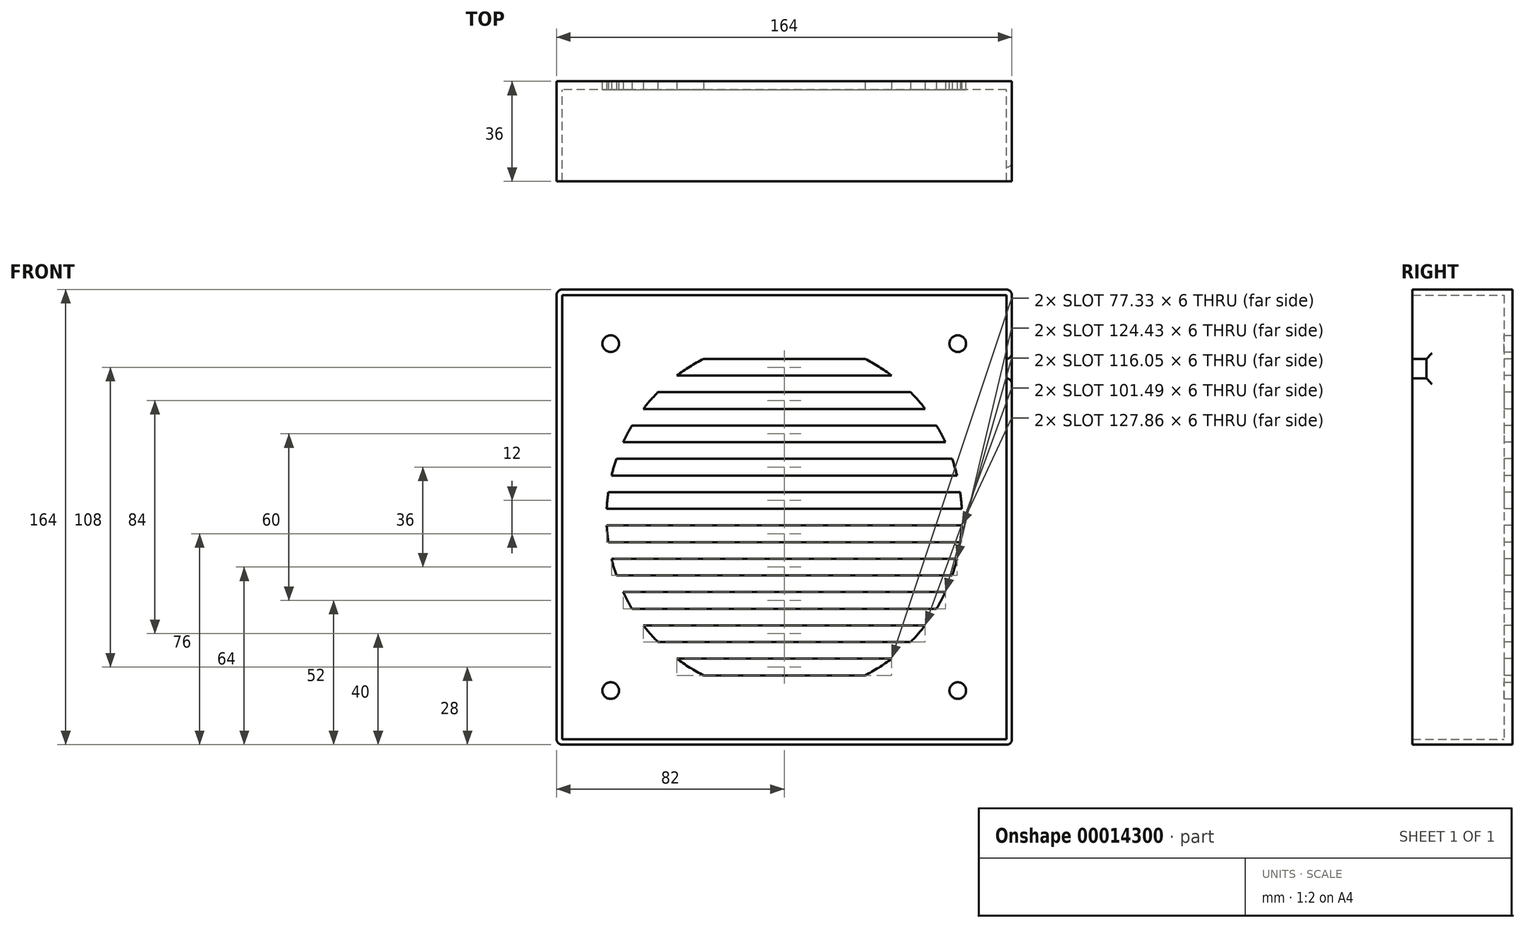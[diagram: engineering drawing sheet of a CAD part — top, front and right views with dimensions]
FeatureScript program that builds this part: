
annotation { "Feature Type Name" : "Feature", "Feature Type Description" : "" }
export const myFeature = defineFeature(function(context is Context, id is Id, definition is map)
    precondition{}
    {
        {
            var Q0;
            Q0=qCreatedBy(makeId("Front.planeOp"),FACE);
            var sketch = newSketch(context, id + "F0", { "sketchPlane" : qUnion([Q0])});
            skLineSegment(sketch, "E0.rect.bottom", {"start": v(-82, 82) * mm, "end": v(82, 82) * mm});
            skLineSegment(sketch, "E0.rect.top", {"start": v(-82, -82) * mm, "end": v(82, -82) * mm});
            skLineSegment(sketch, "E0.rect.left", {"start": v(-82, 82) * mm, "end": v(-82, -82) * mm});
            skLineSegment(sketch, "E0.rect.right", {"start": v(82, 82) * mm, "end": v(82, -82) * mm});
            skPoint(sketch, "E0.rect.middle", {"position": v(0, 0) * mm});
            skCircle(sketch, "E1", {"center": v(-62.5, 62.5) * mm, "radius": 3 * mm});
            skCircle(sketch, "E2", {"center": v(62.5, 62.5) * mm, "radius": 3 * mm});
            skCircle(sketch, "E3", {"center": v(62.5, -62.5) * mm, "radius": 3 * mm});
            skCircle(sketch, "E4", {"center": v(-62.5, -62.5) * mm, "radius": 3 * mm});
            skLineSegment(sketch, "E5", {"start": v(-62.5, 62.5) * mm, "end": v(62.5, 62.5) * mm, "construction": true});
            skLineSegment(sketch, "E6", {"start": v(62.5, 62.5) * mm, "end": v(62.5, -62.5) * mm, "construction": true});
            skLineSegment(sketch, "E7", {"start": v(-62.5, -62.5) * mm, "end": v(62.5, -62.5) * mm, "construction": true});
            skLineSegment(sketch, "E8", {"start": v(-62.5, -62.5) * mm, "end": v(-62.5, 62.5) * mm, "construction": true});
            skLineSegment(sketch, "E9", {"start": v(-62.5, -62.5) * mm, "end": v(-62.5, -82) * mm, "construction": true});
            skLineSegment(sketch, "E10", {"start": v(-62.5, -62.5) * mm, "end": v(-82, -62.5) * mm, "construction": true});
            skLineSegment(sketch, "E11", {"start": v(62.5, 62.5) * mm, "end": v(62.5, 82) * mm, "construction": true});
            skLineSegment(sketch, "E12", {"start": v(62.5, 62.5) * mm, "end": v(82, 62.5) * mm, "construction": true});
            skSolve(sketch);
        }
        {
            var Q0;
            Q0 = qSketchRegion(id + "F0", true);
            extrude(context, id + "F1", {"entities" : qUnion([Q0]), "depth" : 3 * mm});
        }
        {
            var Q0;
            Q0=makeQuery(id+"F1.opExtrude","CAP_FACE",FACE,{"disambiguationData":[OSD([sQuery(id+"F0.wireOp",EDGE,"E0.rect.bottom"),sQuery(id+"F0.wireOp",EDGE,"E0.rect.top"),sQuery(id+"F0.wireOp",EDGE,"E0.rect.left"),sQuery(id+"F0.wireOp",EDGE,"E0.rect.right")])],"isStart":false});
            var sketch = newSketch(context, id + "F2", { "sketchPlane" : qUnion([Q0])});
            skLineSegment(sketch, "E13.rect.bottom", {"start": v(80, 80) * mm, "end": v(-80, 80) * mm});
            skLineSegment(sketch, "E13.rect.top", {"start": v(80, -80) * mm, "end": v(-80, -80) * mm});
            skLineSegment(sketch, "E13.rect.left", {"start": v(80, 80) * mm, "end": v(80, -80) * mm});
            skLineSegment(sketch, "E13.rect.right", {"start": v(-80, 80) * mm, "end": v(-80, -80) * mm});
            skPoint(sketch, "E13.rect.middle", {"position": v(0, 0) * mm});
            skLineSegment(sketch, "E14.rect.bottom", {"start": v(-82, 82) * mm, "end": v(82, 82) * mm});
            skLineSegment(sketch, "E14.rect.top", {"start": v(-82, -82) * mm, "end": v(82, -82) * mm});
            skLineSegment(sketch, "E14.rect.left", {"start": v(-82, 82) * mm, "end": v(-82, -82) * mm});
            skLineSegment(sketch, "E14.rect.right", {"start": v(82, 82) * mm, "end": v(82, -82) * mm});
            skLineSegment(sketch, "E15", {"start": v(-80, 80) * mm, "end": v(-80, 82) * mm, "construction": true});
            skLineSegment(sketch, "E16", {"start": v(-80, 73.83) * mm, "end": v(-82, 73.83) * mm, "construction": true});
            skLineSegment(sketch, "E17", {"start": v(-80, 67.42) * mm, "end": v(80, 67.42) * mm, "construction": true});
            skSolve(sketch);
        }
        {
            var Q0;
            Q0=makeQuery(id+"F2.imprint","IMPRINT",FACE,{"disambiguationData":[TD([[makeQuery(id+"F2.imprint","IMPRINT",EDGE,{"derivedFrom":sQuery(id+"F2.wireOp",EDGE,"E13.rect.bottom")}),-1.0]])]});
            extrude(context, id + "F3", {"entities" : qUnion([Q0]), "operationType" : NewBodyOperationType.ADD, "depth" : 28 * mm});
        }
        {
            var Q0;
            Q0=makeQuery(id+"F1.opExtrude","CAP_FACE",FACE,{"disambiguationData":[OSD([sQuery(id+"F0.wireOp",EDGE,"E0.rect.bottom"),sQuery(id+"F0.wireOp",EDGE,"E0.rect.top"),sQuery(id+"F0.wireOp",EDGE,"E0.rect.left"),sQuery(id+"F0.wireOp",EDGE,"E0.rect.right")])],"isStart":false});
            var sketch = newSketch(context, id + "F4", { "sketchPlane" : qUnion([Q0])});
            skCircle(sketch, "E18", {"center": v(0, 0) * mm, "radius": 64 * mm});
            skLineSegment(sketch, "E19", {"start": v(-63.93, 3) * mm, "end": v(63.93, 3) * mm});
            skLineSegment(sketch, "E20", {"start": v(-63.93, -3) * mm, "end": v(63.93, -3) * mm});
            skLineSegment(sketch, "E21", {"start": v(-63.36, 9) * mm, "end": v(63.36, 9) * mm});
            skLineSegment(sketch, "E22", {"start": v(-62.22, 15) * mm, "end": v(62.22, 15) * mm});
            skLineSegment(sketch, "E23", {"start": v(-63.36, -9) * mm, "end": v(63.36, -9) * mm});
            skLineSegment(sketch, "E24", {"start": v(-60.46, 21) * mm, "end": v(60.46, 21) * mm});
            skLineSegment(sketch, "E25", {"start": v(-58.03, 27) * mm, "end": v(58.03, 27) * mm});
            skLineSegment(sketch, "E26", {"start": v(-50.74, 39) * mm, "end": v(50.74, 39) * mm});
            skLineSegment(sketch, "E27", {"start": v(-45.5, 45) * mm, "end": v(45.5, 45) * mm});
            skLineSegment(sketch, "E28", {"start": v(-38.67, 51) * mm, "end": v(38.67, 51) * mm});
            skLineSegment(sketch, "E29", {"start": v(-29.1, 57) * mm, "end": v(29.1, 57) * mm});
            skLineSegment(sketch, "E30", {"start": v(-62.22, -15) * mm, "end": v(62.22, -15) * mm});
            skLineSegment(sketch, "E31", {"start": v(-60.46, -21) * mm, "end": v(60.46, -21) * mm});
            skLineSegment(sketch, "E32", {"start": v(-58.03, -27) * mm, "end": v(58.03, -27) * mm});
            skLineSegment(sketch, "E33", {"start": v(-54.84, -33) * mm, "end": v(54.84, -33) * mm});
            skLineSegment(sketch, "E34", {"start": v(-50.74, -39) * mm, "end": v(50.74, -39) * mm});
            skLineSegment(sketch, "E35", {"start": v(-45.5, -45) * mm, "end": v(45.5, -45) * mm});
            skLineSegment(sketch, "E36", {"start": v(-38.67, -51) * mm, "end": v(38.67, -51) * mm});
            skLineSegment(sketch, "E37", {"start": v(-29.1, -57) * mm, "end": v(29.1, -57) * mm});
            skLineSegment(sketch, "E38", {"start": v(-54.84, 33) * mm, "end": v(54.84, 33) * mm});
            skSolve(sketch);
        }
        {
            var Q0;
            {var subQ1=sQuery(id+"F4.wireOp",EDGE,"E19");Q0=makeQuery(id+"F4.imprint","IMPRINT",FACE,{"disambiguationData":[TD([[makeQuery(id+"F4.imprint","IMPRINT",EDGE,{"derivedFrom":subQ1}),1.0]])]});}
            var Q1;
            {var subQ1=sQuery(id+"F4.wireOp",EDGE,"E20");Q1=makeQuery(id+"F4.imprint","IMPRINT",FACE,{"disambiguationData":[TD([[makeQuery(id+"F4.imprint","IMPRINT",EDGE,{"derivedFrom":subQ1}),-1.0]])]});}
            var Q2;
            {var subQ0=sQuery(id+"F4.wireOp",EDGE,"E22");Q2=makeQuery(id+"F4.imprint","IMPRINT",FACE,{"disambiguationData":[TD([[makeQuery(id+"F4.imprint","IMPRINT",EDGE,{"derivedFrom":subQ0}),1.0]])]});}
            var Q3;
            {var subQ1=sQuery(id+"F4.wireOp",EDGE,"E30");Q3=makeQuery(id+"F4.imprint","IMPRINT",FACE,{"disambiguationData":[TD([[makeQuery(id+"F4.imprint","IMPRINT",EDGE,{"derivedFrom":subQ1}),-1.0]])]});}
            var Q4;
            {var subQ1=sQuery(id+"F4.wireOp",EDGE,"E32");Q4=makeQuery(id+"F4.imprint","IMPRINT",FACE,{"disambiguationData":[TD([[makeQuery(id+"F4.imprint","IMPRINT",EDGE,{"derivedFrom":subQ1}),-1.0]])]});}
            var Q5;
            {var subQ1=sQuery(id+"F4.wireOp",EDGE,"E34");Q5=makeQuery(id+"F4.imprint","IMPRINT",FACE,{"disambiguationData":[TD([[makeQuery(id+"F4.imprint","IMPRINT",EDGE,{"derivedFrom":subQ1}),-1.0]])]});}
            var Q6;
            {var subQ1=sQuery(id+"F4.wireOp",EDGE,"E36");Q6=makeQuery(id+"F4.imprint","IMPRINT",FACE,{"disambiguationData":[TD([[makeQuery(id+"F4.imprint","IMPRINT",EDGE,{"derivedFrom":subQ1}),-1.0]])]});}
            var Q7;
            {var subQ1=sQuery(id+"F4.wireOp",EDGE,"E25");Q7=makeQuery(id+"F4.imprint","IMPRINT",FACE,{"disambiguationData":[TD([[makeQuery(id+"F4.imprint","IMPRINT",EDGE,{"derivedFrom":subQ1}),1.0]])]});}
            var Q8;
            {var subQ1=sQuery(id+"F4.wireOp",EDGE,"E26");Q8=makeQuery(id+"F4.imprint","IMPRINT",FACE,{"disambiguationData":[TD([[makeQuery(id+"F4.imprint","IMPRINT",EDGE,{"derivedFrom":subQ1}),1.0]])]});}
            var Q9;
            {var subQ1=sQuery(id+"F4.wireOp",EDGE,"E28");Q9=makeQuery(id+"F4.imprint","IMPRINT",FACE,{"disambiguationData":[TD([[makeQuery(id+"F4.imprint","IMPRINT",EDGE,{"derivedFrom":subQ1}),1.0]])]});}
            extrude(context, id + "F5", {"entities" : qUnion([Q0, Q1, Q2, Q3, Q4, Q5, Q6, Q7, Q8, Q9]), "operationType" : NewBodyOperationType.REMOVE, "oppositeDirection" : true, "depth" : 5 * mm});
        }
        {
            var Q0;
            Q0=makeQuery(id+"F3.boolean.opBoolean","MERGE",EDGE,{"derivedFrom":[makeQuery(id+"F1.opExtrude","SWEPT_EDGE",EDGE,{"disambiguationData":[OSD([sQuery(id+"F0.wireOp",EDGE,"E0.rect.bottom"),sQuery(id+"F0.wireOp",EDGE,"E0.rect.left")])]}),makeQuery(id+"F3.opExtrude","SWEPT_EDGE",EDGE,{"disambiguationData":[OSD([sQuery(id+"F2.wireOp",EDGE,"E14.rect.bottom"),sQuery(id+"F2.wireOp",EDGE,"E14.rect.left")])]})]});
            fillet(context, id + "F6", {"entities" : qUnion([Q0]), "radius" : 2 * mm, "tangentPropagation" : true, "allowEdgeOverflow" : false});
        }
        {
            var Q0;
            Q0=makeQuery(id+"F3.boolean.opBoolean","MERGE",EDGE,{"derivedFrom":[makeQuery(id+"F1.opExtrude","SWEPT_EDGE",EDGE,{"disambiguationData":[OSD([sQuery(id+"F0.wireOp",EDGE,"E0.rect.bottom"),sQuery(id+"F0.wireOp",EDGE,"E0.rect.right")])]}),makeQuery(id+"F3.opExtrude","SWEPT_EDGE",EDGE,{"disambiguationData":[OSD([sQuery(id+"F2.wireOp",EDGE,"E14.rect.bottom"),sQuery(id+"F2.wireOp",EDGE,"E14.rect.right")])]})]});
            var Q1;
            Q1=makeQuery(id+"F3.boolean.opBoolean","MERGE",EDGE,{"derivedFrom":[makeQuery(id+"F1.opExtrude","SWEPT_EDGE",EDGE,{"disambiguationData":[OSD([sQuery(id+"F0.wireOp",EDGE,"E0.rect.top"),sQuery(id+"F0.wireOp",EDGE,"E0.rect.left")])]}),makeQuery(id+"F3.opExtrude","SWEPT_EDGE",EDGE,{"disambiguationData":[OSD([sQuery(id+"F2.wireOp",EDGE,"E14.rect.top"),sQuery(id+"F2.wireOp",EDGE,"E14.rect.left")])]})]});
            var Q2;
            Q2=makeQuery(id+"F3.boolean.opBoolean","MERGE",EDGE,{"derivedFrom":[makeQuery(id+"F1.opExtrude","SWEPT_EDGE",EDGE,{"disambiguationData":[OSD([sQuery(id+"F0.wireOp",EDGE,"E0.rect.top"),sQuery(id+"F0.wireOp",EDGE,"E0.rect.right")])]}),makeQuery(id+"F3.opExtrude","SWEPT_EDGE",EDGE,{"disambiguationData":[OSD([sQuery(id+"F2.wireOp",EDGE,"E14.rect.top"),sQuery(id+"F2.wireOp",EDGE,"E14.rect.right")])]})]});
            fillet(context, id + "F7", {"entities" : qUnion([Q0, Q1, Q2]), "radius" : 2 * mm, "tangentPropagation" : true, "allowEdgeOverflow" : false});
        }
        {
            var Q0;
            Q0=makeQuery(id+"F3.opExtrude","CAP_FACE",FACE,{"disambiguationData":[OSD([sQuery(id+"F2.wireOp",EDGE,"E13.rect.bottom"),sQuery(id+"F2.wireOp",EDGE,"E13.rect.top"),sQuery(id+"F2.wireOp",EDGE,"E13.rect.left"),sQuery(id+"F2.wireOp",EDGE,"E13.rect.right"),sQuery(id+"F2.wireOp",EDGE,"E14.rect.bottom"),sQuery(id+"F2.wireOp",EDGE,"E14.rect.top"),sQuery(id+"F2.wireOp",EDGE,"E14.rect.left"),sQuery(id+"F2.wireOp",EDGE,"E14.rect.right")])],"isStart":false});
            var sketch = newSketch(context, id + "F8", { "sketchPlane" : qUnion([Q0])});
            skLineSegment(sketch, "E39", {"start": v(80, 57) * mm, "end": v(82, 57) * mm});
            skLineSegment(sketch, "E40", {"start": v(82, 50) * mm, "end": v(80, 50) * mm});
            skLineSegment(sketch, "E41", {"start": v(80, 57) * mm, "end": v(80, 80) * mm});
            skLineSegment(sketch, "E42", {"start": v(80, 80) * mm, "end": v(-80, 80) * mm});
            skLineSegment(sketch, "E43", {"start": v(-80, 80) * mm, "end": v(-80, -80) * mm});
            skLineSegment(sketch, "E44", {"start": v(-80, -80) * mm, "end": v(80, -80) * mm});
            skLineSegment(sketch, "E45", {"start": v(80, -80) * mm, "end": v(80, 50) * mm});
            skLineSegment(sketch, "E46", {"start": v(82, 50) * mm, "end": v(82, -82) * mm});
            skLineSegment(sketch, "E47", {"start": v(82, -82) * mm, "end": v(-82, -82) * mm});
            skLineSegment(sketch, "E48", {"start": v(-82, -82) * mm, "end": v(-82, 82) * mm});
            skLineSegment(sketch, "E49", {"start": v(-82, 82) * mm, "end": v(82, 82) * mm});
            skLineSegment(sketch, "E50", {"start": v(82, 82) * mm, "end": v(82, 57) * mm});
            skSolve(sketch);
        }
        {
            var Q0;
            Q0 = qSketchRegion(id + "F8", true);
            extrude(context, id + "F9", {"entities" : qUnion([Q0]), "operationType" : NewBodyOperationType.ADD, "depth" : 5 * mm});
        }
        {
            var Q0;
            Q0=makeQuery(id+"F9.opExtrude","SWEPT_EDGE",EDGE,{"disambiguationData":[OSD([sQuery(id+"F8.wireOp",EDGE,"E49"),sQuery(id+"F8.wireOp",EDGE,"E50")])]});
            var Q1;
            Q1=makeQuery(id+"F9.opExtrude","SWEPT_EDGE",EDGE,{"disambiguationData":[OSD([sQuery(id+"F8.wireOp",EDGE,"E48"),sQuery(id+"F8.wireOp",EDGE,"E49")])]});
            var Q2;
            Q2=makeQuery(id+"F9.opExtrude","SWEPT_EDGE",EDGE,{"disambiguationData":[OSD([sQuery(id+"F8.wireOp",EDGE,"E47"),sQuery(id+"F8.wireOp",EDGE,"E48")])]});
            var Q3;
            Q3=makeQuery(id+"F9.opExtrude","SWEPT_EDGE",EDGE,{"disambiguationData":[OSD([sQuery(id+"F8.wireOp",EDGE,"E46"),sQuery(id+"F8.wireOp",EDGE,"E47")])]});
            var Q4;
            Q4=makeQuery(id+"F9.opExtrude","SWEPT_EDGE",EDGE,{"disambiguationData":[OSD([sQuery(id+"F2.wireOp",EDGE,"E14.rect.right"),sQuery(id+"F8.wireOp",EDGE,"E39"),sQuery(id+"F8.wireOp",EDGE,"E50")])]});
            var Q5;
            Q5=makeQuery(id+"F3.opExtrude","CAP_EDGE",EDGE,{"disambiguationData":[OSD([sQuery(id+"F2.wireOp",EDGE,"E14.rect.right")])],"isStart":false});
            var Q6;
            Q6=makeQuery(id+"F9.opExtrude","SWEPT_EDGE",EDGE,{"disambiguationData":[OSD([sQuery(id+"F2.wireOp",EDGE,"E14.rect.right"),sQuery(id+"F8.wireOp",EDGE,"E40"),sQuery(id+"F8.wireOp",EDGE,"E46")])]});
            fillet(context, id + "F10", {"entities" : qUnion([Q0, Q1, Q2, Q3, Q4, Q5, Q6]), "radius" : 2 * mm, "tangentPropagation" : true, "allowEdgeOverflow" : false});
        }
    });
